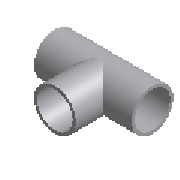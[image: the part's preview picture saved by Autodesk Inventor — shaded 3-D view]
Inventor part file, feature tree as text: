
AUTODESK INVENTOR PART (.ipt)
format: ipt  version: 2023.1 (Build 271208000, 208)  size: 172,032 bytes
history: native  units: mm (DEFAULTED — no unit token found)
features: other x6, extrude x4, sketch x4
ambient origin geometry x8: Origin, YZ Plane, XZ Plane, XY Plane, X Axis, Y Axis, Z Axis, Center Point
bodies: Solid1 (feature_tree)
feature tree (14):
  extrude  "Extrude1"  Depth=286.0mm
  extrude  "Extrude2"  Depth=168.3mm
  extrude  "Extrude3"  TaperAngle=0.0deg  [1 undecoded]
  extrude  "Extrude4"  Depth=143.0mm
  other  "Work Axis1"
  other  "Work Point1"
  other  "Work Axis2"
  other  "Work Point2"
  other  "Work Axis3"
  other  "Work Point3"
  sketch  "Sketch1"  dims[d0=168.3mm d1=286.0mm]
  sketch  "Sketch2"  dims[d2=0.0mm d3=168.3mm]
  sketch  "Sketch3"  dims[d4=143.0mm d5=0.0mm]
  sketch  "Sketch4"  dims[d6=163.1mm d7=143.0mm d8=0.0mm d9=163.1mm d10=143.0mm d11=0.0mm]
note: 1 required parameter value undecoded (feature->parameter linkage not recoverable at this tier; creation-order binding heuristic only, values carry confidence <= 0.55)
